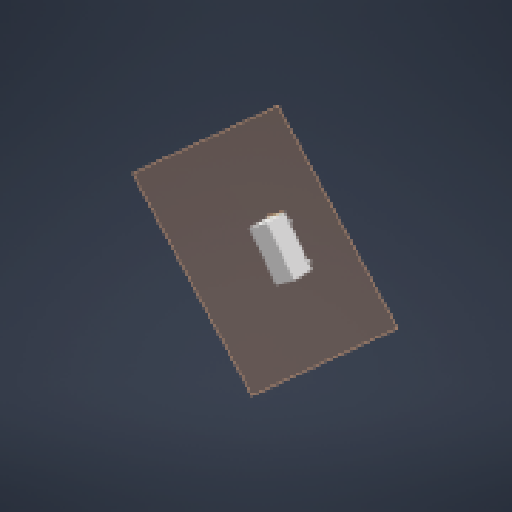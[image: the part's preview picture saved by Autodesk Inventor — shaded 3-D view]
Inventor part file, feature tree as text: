
AUTODESK INVENTOR PART (.ipt)
format: ipt  version: 2024.2 (Build 282272000, 272)  size: 239,616 bytes
history: native  units: in
note: dims shown in document units (in); Inventor stores cm internally (conversion verified against a paired STEP export)
features: other x5, extrude x3, sketch x3, plane x2, fillet x1
ambient origin geometry x8: Origin, YZ Plane, XZ Plane, XY Plane, X Axis, Y Axis, Z Axis, Center Point
bodies: Solid1 (feature_tree)
feature tree (14):
  plane  "Work Plane1"
  extrude  "Extrusion1"  Depth=2.0472in
  extrude  "Extrusion2"  Depth=0.1969in
  fillet  "Fillet1"  Radius=0.1969in
  plane  "Work Plane2"
  extrude  "Extrusion3"  Depth=0.1181in TaperAngle=0.0deg
  sketch  "Sketch1"  dims[d0=4.5669in d1=2.0472in]
  sketch  "Sketch2"  dims[d2=0.0984in d3=0.1575in d4=0.1969in]
  sketch  "Sketch3"  dims[d5=1.8504in d6=0.0in d7=0.1181in d8=0.0in d9=0.0625in d16=0.1693in d18=0.1693in d20=0.75in d21=0.75in d22=0.1181in d23=0.0in d24=0.2in d25=0.125in d26=0.125in d27=0.125in d28=0.2in d29=0.125in d30=0.125in]
  other  "Assembly1"
  other  "Matrix 12V 3000mAh NiMH Battery 14-0014 - Matrix 12V 3000mAh NiMH Battery 14-0014:1"
  other  "<userpath>\Desktop\Robotics\Swerve2\Assemblies\Full_Swerve.iam"
  other  "Full_Swerve.iam"
  other  "Pod_Holders:1"
